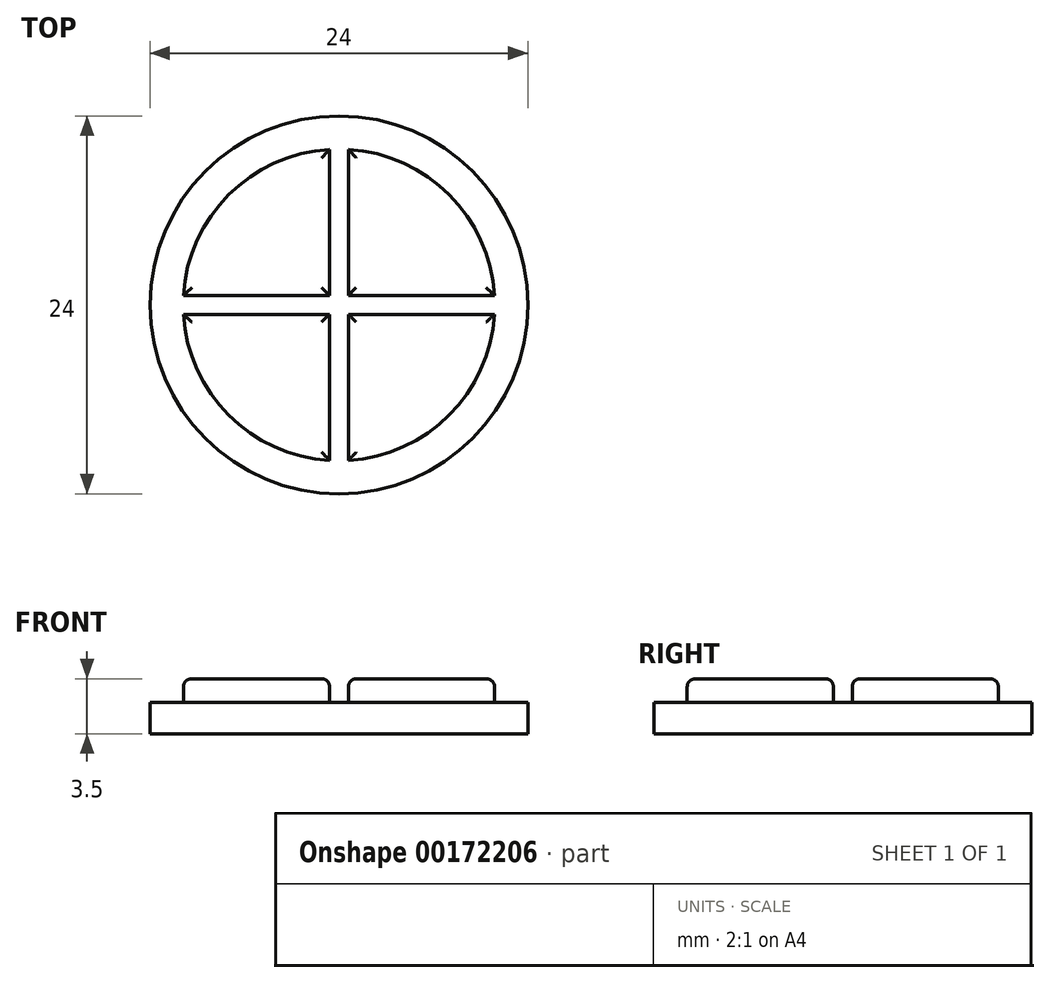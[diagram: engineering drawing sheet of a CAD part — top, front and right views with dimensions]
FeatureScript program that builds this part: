
annotation { "Feature Type Name" : "Feature", "Feature Type Description" : "" }
export const myFeature = defineFeature(function(context is Context, id is Id, definition is map)
    precondition{}
    {
        {
            var Q0;
            Q0=qCreatedBy(makeId("Top.planeOp"),FACE);
            var sketch = newSketch(context, id + "F0", { "sketchPlane" : qUnion([Q0])});
            skCircle(sketch, "E0", {"center": v(0, 0) * mm, "radius": 12 * mm});
            skSolve(sketch);
        }
        {
            var Q0;
            Q0 = qSketchRegion(id + "F0", true);
            extrude(context, id + "F1", {"entities" : qUnion([Q0]), "depth" : 2 * mm});
        }
        {
            var Q0;
            Q0=makeQuery(id+"F1.opExtrude","CAP_FACE",FACE,{"disambiguationData":[OSD([sQuery(id+"F0.wireOp",EDGE,"E0")])],"isStart":false});
            var sketch = newSketch(context, id + "F2", { "sketchPlane" : qUnion([Q0])});
            skCircle(sketch, "E1", {"center": v(0, 0) * mm, "radius": 9.9 * mm});
            skLineSegment(sketch, "E2.bottom", {"start": v(9.88, -0.6) * mm, "end": v(-9.88, -0.6) * mm});
            skLineSegment(sketch, "E2.top", {"start": v(9.88, 0.6) * mm, "end": v(-9.88, 0.6) * mm});
            skLineSegment(sketch, "E2.left", {"start": v(9.88, -0.6) * mm, "end": v(9.88, 0.6) * mm});
            skLineSegment(sketch, "E2.right", {"start": v(-9.88, -0.6) * mm, "end": v(-9.88, 0.6) * mm});
            skLineSegment(sketch, "E3.bottom", {"start": v(0.6, -9.88) * mm, "end": v(-0.6, -9.88) * mm});
            skLineSegment(sketch, "E3.top", {"start": v(0.6, 9.88) * mm, "end": v(-0.6, 9.88) * mm});
            skLineSegment(sketch, "E3.left", {"start": v(0.6, -9.88) * mm, "end": v(0.6, 9.88) * mm});
            skLineSegment(sketch, "E3.right", {"start": v(-0.6, -9.88) * mm, "end": v(-0.6, 9.88) * mm});
            skSolve(sketch);
        }
        {
            var Q0;
            {var subQ0=sQuery(id+"F2.wireOp",EDGE,"E2.bottom");var subQ3=sQuery(id+"F2.wireOp",EDGE,"E3.right");var subQ5=makeQuery(id+"F2.imprint","INTERSECT",VERTEX,{"derivedFrom":[subQ0,subQ3]});Q0=makeQuery(id+"F2.imprint","IMPRINT",FACE,{"disambiguationData":[TD([[makeQuery(id+"F2.imprint","IMPRINT",EDGE,{"disambiguationData":[TD([[subQ5,-1.0]])],"derivedFrom":subQ0}),1.0]])]});}
            var Q1;
            {var subQ0=sQuery(id+"F2.wireOp",EDGE,"E2.top");var subQ3=sQuery(id+"F2.wireOp",EDGE,"E3.right");var subQ5=makeQuery(id+"F2.imprint","INTERSECT",VERTEX,{"derivedFrom":[subQ0,subQ3]});Q1=makeQuery(id+"F2.imprint","IMPRINT",FACE,{"disambiguationData":[TD([[makeQuery(id+"F2.imprint","IMPRINT",EDGE,{"disambiguationData":[TD([[subQ5,-1.0]])],"derivedFrom":subQ0}),-1.0]])]});}
            var Q2;
            {var subQ0=sQuery(id+"F2.wireOp",EDGE,"E2.top");var subQ3=sQuery(id+"F2.wireOp",EDGE,"E3.left");var subQ5=makeQuery(id+"F2.imprint","INTERSECT",VERTEX,{"derivedFrom":[subQ0,subQ3]});Q2=makeQuery(id+"F2.imprint","IMPRINT",FACE,{"disambiguationData":[TD([[makeQuery(id+"F2.imprint","IMPRINT",EDGE,{"disambiguationData":[TD([[subQ5,1.0]])],"derivedFrom":subQ0}),-1.0]])]});}
            var Q3;
            {var subQ0=sQuery(id+"F2.wireOp",EDGE,"E2.bottom");var subQ3=sQuery(id+"F2.wireOp",EDGE,"E3.left");var subQ5=makeQuery(id+"F2.imprint","INTERSECT",VERTEX,{"derivedFrom":[subQ0,subQ3]});Q3=makeQuery(id+"F2.imprint","IMPRINT",FACE,{"disambiguationData":[TD([[makeQuery(id+"F2.imprint","IMPRINT",EDGE,{"disambiguationData":[TD([[subQ5,1.0]])],"derivedFrom":subQ0}),1.0]])]});}
            extrude(context, id + "F3", {"entities" : qUnion([Q0, Q1, Q2, Q3]), "operationType" : NewBodyOperationType.ADD, "depth" : 1.5 * mm});
        }
        {
            var Q0;
            {var subQ0=sQuery(id+"F2.wireOp",EDGE,"E1");Q0=makeQuery(id+"F3.opExtrude","CAP_EDGE",EDGE,{"disambiguationData":[OSD([subQ0]),TDD([makeQuery(id+"F2.imprint","IMPRINT",EDGE,{"disambiguationData":[TD([[makeQuery(id+"F2.imprint","INTERSECT",VERTEX,{"derivedFrom":[subQ0,sQuery(id+"F2.wireOp",EDGE,"E2.bottom"),sQuery(id+"F2.wireOp",EDGE,"E2.right")]}),-1.0]])],"derivedFrom":subQ0})])],"isStart":false});}
            var Q1;
            {var subQ0=sQuery(id+"F2.wireOp",EDGE,"E3.right");Q1=makeQuery(id+"F3.opExtrude","CAP_EDGE",EDGE,{"disambiguationData":[OSD([subQ0]),TDD([makeQuery(id+"F2.imprint","IMPRINT",EDGE,{"disambiguationData":[TD([[makeQuery(id+"F2.imprint","INTERSECT",VERTEX,{"derivedFrom":[sQuery(id+"F2.wireOp",EDGE,"E2.bottom"),subQ0]}),1.0]])],"derivedFrom":subQ0})])],"isStart":false});}
            var Q2;
            {var subQ0=sQuery(id+"F2.wireOp",EDGE,"E2.bottom");Q2=makeQuery(id+"F3.opExtrude","CAP_EDGE",EDGE,{"disambiguationData":[OSD([subQ0]),TDD([makeQuery(id+"F2.imprint","IMPRINT",EDGE,{"disambiguationData":[TD([[makeQuery(id+"F2.imprint","INTERSECT",VERTEX,{"derivedFrom":[subQ0,sQuery(id+"F2.wireOp",EDGE,"E3.right")]}),-1.0]])],"derivedFrom":subQ0})])],"isStart":false});}
            var Q3;
            {var subQ0=sQuery(id+"F2.wireOp",EDGE,"E2.top");Q3=makeQuery(id+"F3.opExtrude","CAP_EDGE",EDGE,{"disambiguationData":[OSD([subQ0]),TDD([makeQuery(id+"F2.imprint","IMPRINT",EDGE,{"disambiguationData":[TD([[makeQuery(id+"F2.imprint","INTERSECT",VERTEX,{"derivedFrom":[subQ0,sQuery(id+"F2.wireOp",EDGE,"E3.right")]}),-1.0]])],"derivedFrom":subQ0})])],"isStart":false});}
            var Q4;
            {var subQ0=sQuery(id+"F2.wireOp",EDGE,"E3.right");Q4=makeQuery(id+"F3.opExtrude","CAP_EDGE",EDGE,{"disambiguationData":[OSD([subQ0]),TDD([makeQuery(id+"F2.imprint","IMPRINT",EDGE,{"disambiguationData":[TD([[makeQuery(id+"F2.imprint","INTERSECT",VERTEX,{"derivedFrom":[sQuery(id+"F2.wireOp",EDGE,"E2.top"),subQ0]}),-1.0]])],"derivedFrom":subQ0})])],"isStart":false});}
            var Q5;
            {var subQ0=sQuery(id+"F2.wireOp",EDGE,"E2.top");Q5=makeQuery(id+"F3.opExtrude","CAP_EDGE",EDGE,{"disambiguationData":[OSD([subQ0]),TDD([makeQuery(id+"F2.imprint","IMPRINT",EDGE,{"disambiguationData":[TD([[makeQuery(id+"F2.imprint","INTERSECT",VERTEX,{"derivedFrom":[subQ0,sQuery(id+"F2.wireOp",EDGE,"E3.left")]}),1.0]])],"derivedFrom":subQ0})])],"isStart":false});}
            var Q6;
            {var subQ0=sQuery(id+"F2.wireOp",EDGE,"E3.left");Q6=makeQuery(id+"F3.opExtrude","CAP_EDGE",EDGE,{"disambiguationData":[OSD([subQ0]),TDD([makeQuery(id+"F2.imprint","IMPRINT",EDGE,{"disambiguationData":[TD([[makeQuery(id+"F2.imprint","INTERSECT",VERTEX,{"derivedFrom":[sQuery(id+"F2.wireOp",EDGE,"E2.top"),subQ0]}),-1.0]])],"derivedFrom":subQ0})])],"isStart":false});}
            var Q7;
            {var subQ0=sQuery(id+"F2.wireOp",EDGE,"E2.bottom");Q7=makeQuery(id+"F3.opExtrude","CAP_EDGE",EDGE,{"disambiguationData":[OSD([subQ0]),TDD([makeQuery(id+"F2.imprint","IMPRINT",EDGE,{"disambiguationData":[TD([[makeQuery(id+"F2.imprint","INTERSECT",VERTEX,{"derivedFrom":[subQ0,sQuery(id+"F2.wireOp",EDGE,"E3.left")]}),1.0]])],"derivedFrom":subQ0})])],"isStart":false});}
            var Q8;
            {var subQ0=sQuery(id+"F2.wireOp",EDGE,"E3.left");Q8=makeQuery(id+"F3.opExtrude","CAP_EDGE",EDGE,{"disambiguationData":[OSD([subQ0]),TDD([makeQuery(id+"F2.imprint","IMPRINT",EDGE,{"disambiguationData":[TD([[makeQuery(id+"F2.imprint","INTERSECT",VERTEX,{"derivedFrom":[sQuery(id+"F2.wireOp",EDGE,"E2.bottom"),subQ0]}),1.0]])],"derivedFrom":subQ0})])],"isStart":false});}
            var Q9;
            {var subQ0=sQuery(id+"F2.wireOp",EDGE,"E1");Q9=makeQuery(id+"F3.opExtrude","CAP_EDGE",EDGE,{"disambiguationData":[OSD([subQ0]),TDD([makeQuery(id+"F2.imprint","IMPRINT",EDGE,{"disambiguationData":[TD([[makeQuery(id+"F2.imprint","INTERSECT",VERTEX,{"derivedFrom":[subQ0,sQuery(id+"F2.wireOp",EDGE,"E2.bottom"),sQuery(id+"F2.wireOp",EDGE,"E2.left")]}),1.0]])],"derivedFrom":subQ0})])],"isStart":false});}
            var Q10;
            {var subQ0=sQuery(id+"F2.wireOp",EDGE,"E1");Q10=makeQuery(id+"F3.opExtrude","CAP_EDGE",EDGE,{"disambiguationData":[OSD([subQ0]),TDD([makeQuery(id+"F2.imprint","IMPRINT",EDGE,{"disambiguationData":[TD([[makeQuery(id+"F2.imprint","INTERSECT",VERTEX,{"derivedFrom":[subQ0,sQuery(id+"F2.wireOp",EDGE,"E2.top"),sQuery(id+"F2.wireOp",EDGE,"E2.left")]}),-1.0]])],"derivedFrom":subQ0})])],"isStart":false});}
            var Q11;
            {var subQ0=sQuery(id+"F2.wireOp",EDGE,"E1");Q11=makeQuery(id+"F3.opExtrude","CAP_EDGE",EDGE,{"disambiguationData":[OSD([subQ0]),TDD([makeQuery(id+"F2.imprint","IMPRINT",EDGE,{"disambiguationData":[TD([[makeQuery(id+"F2.imprint","INTERSECT",VERTEX,{"derivedFrom":[subQ0,sQuery(id+"F2.wireOp",EDGE,"E2.top"),sQuery(id+"F2.wireOp",EDGE,"E2.right")]}),1.0]])],"derivedFrom":subQ0})])],"isStart":false});}
            fillet(context, id + "F4", {"entities" : qUnion([Q0, Q1, Q2, Q3, Q4, Q5, Q6, Q7, Q8, Q9, Q10, Q11]), "radius" : 0.5 * mm, "tangentPropagation" : true, "allowEdgeOverflow" : false});
        }
    });
